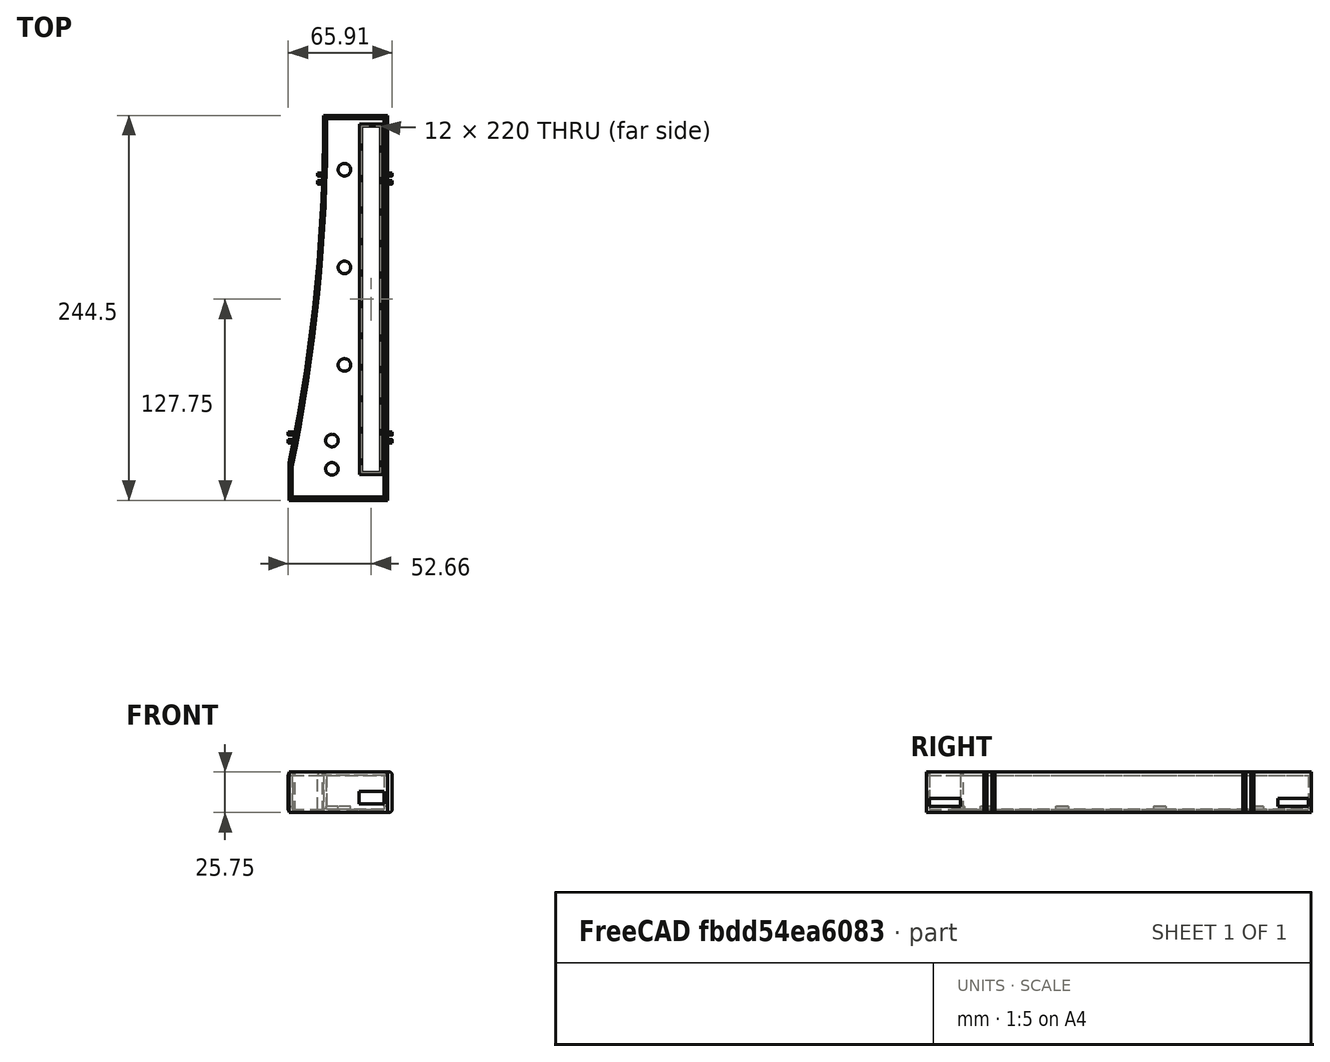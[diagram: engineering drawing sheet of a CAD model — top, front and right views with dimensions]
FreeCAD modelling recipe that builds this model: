
FCSTD DOCUMENT  (FreeCAD 0.19R)
Label: case-bottom
License: All rights reserved
LicenseURL: http://en.wikipedia.org/wiki/All_rights_reserved
objects: Sketcher::SketchObject×10, PartDesign::Pocket×7, PartDesign::Pad×3, Image::ImagePlane×1, PartDesign::Fillet×1, PartDesign::Body×1, Mesh::Feature×1
note: 33 computed .brp shape members not serialized (recipe doc carries the construction recipe); baked Part::Feature solids carry a one-line shape summary decoded from their .brp

FEATURE [Sketcher::SketchObject] Sketch
  FullyConstrained = true
  MapMode = 5
  Support = -> [XY_Plane]
  sketch-geometry (5):
    g0: LineSegment StartX=70.75 StartY=0 StartZ=0 EndX=70.75 EndY=244.5 EndZ=0
    g1: LineSegment StartX=70.75 StartY=244.5 StartZ=0 EndX=30.25 EndY=244.5 EndZ=0
    g2: LineSegment StartX=70.75 StartY=0 StartZ=0 EndX=8.25 EndY=0 EndZ=0
    g3: LineSegment StartX=8.25 StartY=0 StartZ=0 EndX=8.25 EndY=23.5 EndZ=0
    g4: ArcOfCircle CenterX=-1044.74 CenterY=239.918 CenterZ=0 NormalX=0 NormalY=0 NormalZ=1 AngleXU=0 Radius=1075 StartAngle=6.08048 EndAngle=6.28745
  constraints (16):
    c: PointOnObject(g0,g-1)
    c: Vertical(g0)
    c: Coincident(g1,g0)
    c: Horizontal(g1)
    c: Coincident(g2,g0)
    c: PointOnObject(g2,g-1)
    c: Coincident(g3,g2)
    c: Vertical(g3)
    c: Coincident(g4,g3)
    c: Coincident(g4,g1)
    c: DistanceX(g-1,g2) = 8.25
    c: DistanceX(g2,g2) = 62.5
    c: DistanceY(g0,g0) = 244.5
    c: DistanceX(g1,g1) = 40.5
    c: DistanceY(g3,g3) = 23.5
    c: Diameter(g4) = 2150
FEATURE [PartDesign::Pad] Pad
  Direction = (1,1,1)
  Length = 25.75
  Length2 = 100
  Profile = -> Sketch
  Type = 0
FEATURE [Sketcher::SketchObject] Sketch001
  FullyConstrained = true
  MapMode = 5
  Placement = pos=(0,0,25.75) rot=(0,0,1;0rad)
  Support = -> [Pad]
  sketch-geometry (5):
    g0: LineSegment StartX=10.25 StartY=2 StartZ=0 EndX=68.75 EndY=2 EndZ=0
    g1: LineSegment StartX=68.75 StartY=2 StartZ=0 EndX=68.75 EndY=242.5 EndZ=0
    g2: LineSegment StartX=68.75 StartY=242.5 StartZ=0 EndX=32.25 EndY=242.5 EndZ=0
    g3: ArcOfCircle CenterX=-1042.74 CenterY=237.918 CenterZ=0 NormalX=0 NormalY=0 NormalZ=1 AngleXU=0 Radius=1075 StartAngle=6.08048 EndAngle=6.28745
    g4: LineSegment StartX=10.25 StartY=2 StartZ=0 EndX=10.25 EndY=21.5 EndZ=0
  constraints (16):
    c: Horizontal(g0)
    c: Coincident(g1,g0)
    c: Vertical(g1)
    c: DistanceX(g-1,g0) = 10.25
    c: DistanceY(g-1,g0) = 2
    c: DistanceX(g0,g0) = 58.5
    c: Coincident(g2,g1)
    c: Horizontal(g2)
    c: Coincident(g3,g2)
    c: Coincident(g4,g0)
    c: Vertical(g4)
    c: Coincident(g3,g4)
    c: DistanceY(g1,g1) = 240.5
    c: DistanceX(g2,g2) = 36.5
    c: DistanceY(g4,g4) = 19.5
    c: Diameter(g3) = 2150
FEATURE [PartDesign::Pocket] Pocket
  BaseFeature = -> Pad
  Length = 23.75
  Length2 = 100
  Profile = -> Sketch001
  Type = 0
FEATURE [Image::ImagePlane] ImagePlane
  Placement = pos=(39.5,122.25,0) rot=(0,0,1;0rad)
  XSize = 74
  YSize = 240
FEATURE [Sketcher::SketchObject] Sketch002
  FullyConstrained = true
  MapMode = 5
  Placement = pos=(0,0,25.75) rot=(0,0,1;0rad)
  Support = -> [Pocket]
  sketch-geometry (4):
    g0: LineSegment StartX=8.25 StartY=2 StartZ=0 EndX=10.25 EndY=2 EndZ=0
    g1: LineSegment StartX=10.25 StartY=2 StartZ=0 EndX=10.25 EndY=21.5 EndZ=0
    g2: LineSegment StartX=10.25 StartY=21.5 StartZ=0 EndX=8.25 EndY=21.5 EndZ=0
    g3: LineSegment StartX=8.25 StartY=21.5 StartZ=0 EndX=8.25 EndY=2 EndZ=0
  constraints (12):
    c: Coincident(g0,g1)
    c: Coincident(g1,g2)
    c: Coincident(g2,g3)
    c: Coincident(g3,g0)
    c: Horizontal(g0)
    c: Horizontal(g2)
    c: Vertical(g1)
    c: Vertical(g3)
    c: DistanceX(g-1,g0) = 8.25
    c: DistanceY(g-1,g0) = 2
    c: DistanceX(g2,g2) = 2
    c: DistanceY(g1,g1) = 19.5
FEATURE [PartDesign::Pocket] Pocket001
  BaseFeature = -> Pocket
  Length = 21.75
  Length2 = 100
  Profile = -> Sketch002
  Type = 0
FEATURE [Sketcher::SketchObject] Sketch003
  FullyConstrained = true
  MapMode = 5
  Placement = pos=(70.75,0,0) rot=(0.57735,0.57735,0.57735;2.0944rad)
  Support = -> [Pocket001]
  sketch-geometry (8):
    g0: LineSegment StartX=2 StartY=4 StartZ=0 EndX=21.5 EndY=4 EndZ=0
    g1: LineSegment StartX=21.5 StartY=4 StartZ=0 EndX=21.5 EndY=9 EndZ=0
    g2: LineSegment StartX=21.5 StartY=9 StartZ=0 EndX=2 EndY=9 EndZ=0
    g3: LineSegment StartX=2 StartY=9 StartZ=0 EndX=2 EndY=4 EndZ=0
    g4: LineSegment StartX=242.5 StartY=4 StartZ=0 EndX=223 EndY=4 EndZ=0
    g5: LineSegment StartX=223 StartY=4 StartZ=0 EndX=223 EndY=9 EndZ=0
    g6: LineSegment StartX=223 StartY=9 StartZ=0 EndX=242.5 EndY=9 EndZ=0
    g7: LineSegment StartX=242.5 StartY=9 StartZ=0 EndX=242.5 EndY=4 EndZ=0
  constraints (24):
    c: Coincident(g0,g1)
    c: Coincident(g1,g2)
    c: Coincident(g2,g3)
    c: Coincident(g3,g0)
    c: Horizontal(g0)
    c: Horizontal(g2)
    c: Vertical(g1)
    c: Vertical(g3)
    c: Coincident(g4,g5)
    c: Coincident(g5,g6)
    c: Coincident(g6,g7)
    c: Coincident(g7,g4)
    c: Horizontal(g4)
    c: Horizontal(g6)
    c: Vertical(g5)
    c: Vertical(g7)
    c: DistanceX(g-1,g0) = 2
    c: DistanceY(g-1,g0) = 4
    c: DistanceX(g2,g2) = 19.5
    c: DistanceY(g1,g1) = 5
    c: DistanceY(g-1,g4) = 4
    c: DistanceX(g-1,g4) = 223
    c: DistanceX(g6,g6) = 19.5
    c: DistanceY(g7,g7) = 5
FEATURE [PartDesign::Pocket] Pocket002
  BaseFeature = -> Pocket001
  Length = 5
  Length2 = 100
  Profile = -> Sketch003
  Type = 2
FEATURE [Sketcher::SketchObject] Sketch004
  FullyConstrained = true
  MapMode = 5
  Placement = pos=(0,0,0) rot=(1,0,0;1.5708rad)
  Support = -> [Pocket002]
  sketch-geometry (4):
    g0: LineSegment StartX=68.75 StartY=5.5 StartZ=0 EndX=52.75 EndY=5.5 EndZ=0
    g1: LineSegment StartX=52.75 StartY=5.5 StartZ=0 EndX=52.75 EndY=13.5 EndZ=0
    g2: LineSegment StartX=52.75 StartY=13.5 StartZ=0 EndX=68.75 EndY=13.5 EndZ=0
    g3: LineSegment StartX=68.75 StartY=13.5 StartZ=0 EndX=68.75 EndY=5.5 EndZ=0
  constraints (12):
    c: Coincident(g0,g1)
    c: Coincident(g1,g2)
    c: Coincident(g2,g3)
    c: Coincident(g3,g0)
    c: Horizontal(g0)
    c: Horizontal(g2)
    c: Vertical(g1)
    c: Vertical(g3)
    c: DistanceY(g-1,g0) = 5.5
    c: DistanceX(g-1,g0) = 52.75
    c: DistanceY(g3,g3) = 8
    c: DistanceX(g2,g2) = 16
FEATURE [PartDesign::Pocket] Pocket003
  BaseFeature = -> Pocket002
  Length = 5
  Length2 = 100
  Profile = -> Sketch004
  Type = 2
FEATURE [Sketcher::SketchObject] Sketch005
  FullyConstrained = true
  MapMode = 5
  Placement = pos=(0,0,4) rot=(0,0,1;0rad)
  Support = -> [Pocket003]
  sketch-geometry (4):
    g0: LineSegment StartX=66.5 StartY=17.75 StartZ=0 EndX=54.5 EndY=17.75 EndZ=0
    g1: LineSegment StartX=54.5 StartY=17.75 StartZ=0 EndX=54.5 EndY=237.75 EndZ=0
    g2: LineSegment StartX=54.5 StartY=237.75 StartZ=0 EndX=66.5 EndY=237.75 EndZ=0
    g3: LineSegment StartX=66.5 StartY=237.75 StartZ=0 EndX=66.5 EndY=17.75 EndZ=0
  constraints (12):
    c: Coincident(g0,g1)
    c: Coincident(g1,g2)
    c: Coincident(g2,g3)
    c: Coincident(g3,g0)
    c: Horizontal(g0)
    c: Horizontal(g2)
    c: Vertical(g1)
    c: Vertical(g3)
    c: DistanceX(g2,g2) = 12
    c: DistanceY(g3,g3) = 220
    c: DistanceX(g-1,g0) = 54.5
    c: DistanceY(g-1,g0) = 17.75
FEATURE [PartDesign::Pocket] Pocket004
  BaseFeature = -> Pocket003
  Length = 5
  Length2 = 100
  Profile = -> Sketch005
  Type = 1
FEATURE [Sketcher::SketchObject] Sketch006
  FullyConstrained = true
  MapMode = 5
  Placement = pos=(0,0,2) rot=(0,0,1;0rad)
  Support = -> [Pocket004]
  sketch-geometry (4):
    g0: LineSegment StartX=67.75 StartY=16.5 StartZ=0 EndX=53.25 EndY=16.5 EndZ=0
    g1: LineSegment StartX=53.25 StartY=16.5 StartZ=0 EndX=53.25 EndY=239 EndZ=0
    g2: LineSegment StartX=53.25 StartY=239 StartZ=0 EndX=67.75 EndY=239 EndZ=0
    g3: LineSegment StartX=67.75 StartY=239 StartZ=0 EndX=67.75 EndY=16.5 EndZ=0
  constraints (12):
    c: Coincident(g0,g1)
    c: Coincident(g1,g2)
    c: Coincident(g2,g3)
    c: Coincident(g3,g0)
    c: Horizontal(g0)
    c: Horizontal(g2)
    c: Vertical(g1)
    c: Vertical(g3)
    c: DistanceX(g2,g2) = 14.5
    c: DistanceY(g3,g3) = 222.5
    c: DistanceX(g-1,g0) = 53.25
    c: DistanceY(g-1,g0) = 16.5
FEATURE [PartDesign::Pocket] Pocket005
  BaseFeature = -> Pocket004
  Length = 1.25
  Length2 = 100
  Profile = -> Sketch006
  Type = 0
FEATURE [Sketcher::SketchObject] Sketch007
  FullyConstrained = true
  MapMode = 5
  Placement = pos=(0,0,25.75) rot=(0,0,1;0rad)
  Support = -> [Pocket005]
  sketch-geometry (5):
    g0: LineSegment StartX=9.25 StartY=1 StartZ=0 EndX=9.25 EndY=22.5 EndZ=0
    g1: LineSegment StartX=9.25 StartY=1 StartZ=0 EndX=69.75 EndY=1 EndZ=0
    g2: LineSegment StartX=69.75 StartY=1 StartZ=0 EndX=69.75 EndY=243.5 EndZ=0
    g3: LineSegment StartX=69.75 StartY=243.5 StartZ=0 EndX=31.25 EndY=243.5 EndZ=0
    g4: ArcOfCircle CenterX=-1043.74 CenterY=238.918 CenterZ=0 NormalX=0 NormalY=0 NormalZ=1 AngleXU=0 Radius=1075 StartAngle=6.08048 EndAngle=6.28745
  constraints (16):
    c: Vertical(g0)
    c: Coincident(g1,g0)
    c: Horizontal(g1)
    c: Coincident(g2,g1)
    c: Vertical(g2)
    c: Coincident(g3,g2)
    c: Horizontal(g3)
    c: Coincident(g4,g0)
    c: Coincident(g4,g3)
    c: DistanceY(g-1,g0) = 1
    c: DistanceX(g-1,g0) = 9.25
    c: DistanceX(g1,g1) = 60.5
    c: DistanceY(g0,g0) = 21.5
    c: DistanceY(g2,g2) = 242.5
    c: DistanceX(g3,g3) = 38.5
    c: Diameter(g4) = 2150
FEATURE [PartDesign::Pocket] Pocket006
  BaseFeature = -> Pocket005
  Length = 2.25
  Length2 = 100
  Profile = -> Sketch007
  Type = 0
FEATURE [Sketcher::SketchObject] Sketch008
  FullyConstrained = true
  MapMode = 5
  Placement = pos=(0,0,2) rot=(0,0,1;0rad)
  Support = -> [Pocket006]
  sketch-geometry (8):
    g0: Circle CenterX=35.5 CenterY=38 CenterZ=0 NormalX=0 NormalY=0 NormalZ=1 AngleXU=0 Radius=4
    g1: Circle CenterX=43.5 CenterY=86 CenterZ=0 NormalX=0 NormalY=0 NormalZ=1 AngleXU=0 Radius=4
    g2: Circle CenterX=43.5 CenterY=148 CenterZ=0 NormalX=0 NormalY=0 NormalZ=1 AngleXU=0 Radius=4
    g3: Circle CenterX=43.5 CenterY=210 CenterZ=0 NormalX=0 NormalY=0 NormalZ=1 AngleXU=0 Radius=4
    g4: LineSegment StartX=0 StartY=12 StartZ=0 EndX=43.5 EndY=12 EndZ=0
    g5: LineSegment StartX=35.5 StartY=12 StartZ=0 EndX=35.5 EndY=38 EndZ=0
    g6: LineSegment StartX=43.5 StartY=12 StartZ=0 EndX=43.5 EndY=210 EndZ=0
    g7: Circle CenterX=35.5 CenterY=20 CenterZ=0 NormalX=0 NormalY=0 NormalZ=1 AngleXU=0 Radius=4
  constraints (24):
    c: Equal(g1,g2)
    c: Equal(g2,g3)
    c: PointOnObject(g4,g-2)
    c: Horizontal(g4)
    c: PointOnObject(g5,g4)
    c: Coincident(g5,g0)
    c: Vertical(g5)
    c: Coincident(g6,g4)
    c: Coincident(g6,g3)
    c: Vertical(g6)
    c: PointOnObject(g2,g6)
    c: PointOnObject(g1,g6)
    c: DistanceX(g4,g4) = 43.5
    c: DistanceY(g-1,g4) = 12
    c: PointOnObject(g7,g5)
    c: DistanceY(g5,g7) = 8
    c: Equal(g7,g0)
    c: Diameter(g7) = 8
    c: DistanceY(g5,g5) = 26
    c: DistanceX(g4,g5) = 35.5
    c: DistanceY(g6,g6) = 198
    c: DistanceY(g4,g1) = 74
    c: DistanceY(g4,g2) = 136
    c: Equal(g1,g0)
FEATURE [PartDesign::Pad] Pad001
  BaseFeature = -> Pocket006
  Direction = (1,1,1)
  Length = 1.75
  Length2 = 100
  Profile = -> Sketch008
  Type = 0
FEATURE [Sketcher::SketchObject] Sketch009
  FullyConstrained = true
  MapMode = 5
  Placement = pos=(0,0,0) rot=(1,0,0;3.14159rad)
  Support = -> [Pad001]
  sketch-geometry (47):
    g0: LineSegment StartX=8.25 StartY=0 StartZ=0 EndX=70.75 EndY=0 EndZ=0
    g1: LineSegment StartX=70.75 StartY=0 StartZ=0 EndX=70.75 EndY=-244.5 EndZ=0
    g2: LineSegment StartX=70.75 StartY=-244.5 StartZ=0 EndX=30.25 EndY=-244.5 EndZ=0
    g3: LineSegment StartX=8.25 StartY=0 StartZ=0 EndX=8.25 EndY=-23.5 EndZ=0
    g4: ArcOfCircle CenterX=-1044.74 CenterY=-239.918 CenterZ=0 NormalX=0 NormalY=0 NormalZ=1 AngleXU=0 Radius=1075 StartAngle=6.27892 EndAngle=6.48589
    g5: LineSegment StartX=70.75 StartY=-40 StartZ=0 EndX=11.5069 EndY=-40 EndZ=0
    g6: LineSegment StartX=70.75 StartY=-204.5 StartZ=0 EndX=29.6762 EndY=-204.5 EndZ=0
    g7: LineSegment StartX=70.75 StartY=-38.5 StartZ=0 EndX=73.75 EndY=-38.5 EndZ=0
    g8: LineSegment StartX=73.75 StartY=-38.5 StartZ=0 EndX=73.75 EndY=-36.5 EndZ=0
    g9: LineSegment StartX=73.75 StartY=-36.5 StartZ=0 EndX=70.75 EndY=-36.5 EndZ=0
    g10: LineSegment StartX=70.75 StartY=-36.5 StartZ=0 EndX=70.75 EndY=-38.5 EndZ=0
    g11: LineSegment StartX=70.75 StartY=-41.5 StartZ=0 EndX=73.75 EndY=-41.5 EndZ=0
    g12: LineSegment StartX=73.75 StartY=-41.5 StartZ=0 EndX=73.75 EndY=-43.5 EndZ=0
    g13: LineSegment StartX=73.75 StartY=-43.5 StartZ=0 EndX=70.75 EndY=-43.5 EndZ=0
    g14: LineSegment StartX=70.75 StartY=-43.5 StartZ=0 EndX=70.75 EndY=-41.5 EndZ=0
    g15: LineSegment StartX=11.2219 StartY=-38.5 StartZ=0 EndX=7.83842 EndY=-38.5 EndZ=0
    g16: LineSegment StartX=7.83842 StartY=-38.5 StartZ=0 EndX=7.83842 EndY=-36.5 EndZ=0
    g17: LineSegment StartX=7.83842 StartY=-36.5 StartZ=0 EndX=10.8384 EndY=-36.5 EndZ=0
    g18: LineSegment StartX=12.1633 StartY=-43.5 StartZ=0 EndX=7.83842 EndY=-43.5 EndZ=0
    g19: LineSegment StartX=7.83842 StartY=-43.5 StartZ=0 EndX=7.83842 EndY=-41.5 EndZ=0
    g20: LineSegment StartX=7.83842 StartY=-41.5 StartZ=0 EndX=11.7897 EndY=-41.5 EndZ=0
    g21: LineSegment StartX=7.83842 StartY=-41.5 StartZ=0 EndX=7.83842 EndY=-38.5 EndZ=0
    g22: ArcOfCircle CenterX=-1044.74 CenterY=-239.918 CenterZ=0 NormalX=0 NormalY=0 NormalZ=1 AngleXU=0 Radius=1075 StartAngle=0.188479 EndAngle=0.190373
    g23: ArcOfCircle CenterX=-1044.74 CenterY=-239.918 CenterZ=0 NormalX=0 NormalY=0 NormalZ=1 AngleXU=0 Radius=1075 StartAngle=0.183746 EndAngle=0.185639
    g24: LineSegment StartX=11.5069 StartY=-40 StartZ=0 EndX=7.83842 EndY=-40 EndZ=0
    g25: LineSegment StartX=73.75 StartY=-41.5 StartZ=0 EndX=73.75 EndY=-38.5 EndZ=0
    g26: LineSegment StartX=70.75 StartY=-40 StartZ=0 EndX=73.75 EndY=-40 EndZ=0
    g27: LineSegment StartX=70.75 StartY=-204.5 StartZ=0 EndX=73.75 EndY=-204.5 EndZ=0
    g28: LineSegment StartX=73.75 StartY=-206 StartZ=0 EndX=73.75 EndY=-203 EndZ=0
    g29: LineSegment StartX=29.6762 StartY=-204.5 StartZ=0 EndX=26.5551 EndY=-204.5 EndZ=0
    g30: LineSegment StartX=26.5551 StartY=-206 StartZ=0 EndX=26.5551 EndY=-203 EndZ=0
    g31: LineSegment StartX=73.75 StartY=-203 StartZ=0 EndX=70.75 EndY=-203 EndZ=0
    g32: LineSegment StartX=70.75 StartY=-203 StartZ=0 EndX=70.75 EndY=-201 EndZ=0
    g33: LineSegment StartX=70.75 StartY=-201 StartZ=0 EndX=73.75 EndY=-201 EndZ=0
    g34: LineSegment StartX=73.75 StartY=-201 StartZ=0 EndX=73.75 EndY=-203 EndZ=0
    g35: LineSegment StartX=73.75 StartY=-206 StartZ=0 EndX=70.75 EndY=-206 EndZ=0
    g36: LineSegment StartX=70.75 StartY=-206 StartZ=0 EndX=70.75 EndY=-208 EndZ=0
    g37: LineSegment StartX=70.75 StartY=-208 StartZ=0 EndX=73.75 EndY=-208 EndZ=0
    g38: LineSegment StartX=73.75 StartY=-208 StartZ=0 EndX=73.75 EndY=-206 EndZ=0
    g39: LineSegment StartX=26.5551 StartY=-203 StartZ=0 EndX=29.6257 EndY=-203 EndZ=0
    g40: LineSegment StartX=29.5551 StartY=-201 StartZ=0 EndX=26.5551 EndY=-201 EndZ=0
    g41: LineSegment StartX=26.5551 StartY=-201 StartZ=0 EndX=26.5551 EndY=-203 EndZ=0
    g42: LineSegment StartX=26.5551 StartY=-206 StartZ=0 EndX=29.7246 EndY=-206 EndZ=0
    g43: LineSegment StartX=29.7858 StartY=-208 StartZ=0 EndX=26.5551 EndY=-208 EndZ=0
    g44: LineSegment StartX=26.5551 StartY=-208 StartZ=0 EndX=26.5551 EndY=-206 EndZ=0
    g45: ArcOfCircle CenterX=-1044.74 CenterY=-239.918 CenterZ=0 NormalX=0 NormalY=0 NormalZ=1 AngleXU=0 Radius=1075 StartAngle=0.0343487 EndAngle=0.0362103
    g46: ArcOfCircle CenterX=-1044.74 CenterY=-239.918 CenterZ=0 NormalX=0 NormalY=0 NormalZ=1 AngleXU=0 Radius=1075 StartAngle=0.0296951 EndAngle=0.0315565
  constraints (140):
    c: PointOnObject(g0,g-1)
    c: PointOnObject(g0,g-1)
    c: Coincident(g1,g0)
    c: Vertical(g1)
    c: Coincident(g2,g1)
    c: Horizontal(g2)
    c: Coincident(g3,g0)
    c: Vertical(g3)
    c: Coincident(g4,g3)
    c: Coincident(g4,g2)
    c: DistanceX(g-1,g0) = 8.25
    c: DistanceX(g0,g0) = 62.5
    c: DistanceY(g3,g3) = 23.5
    c: DistanceY(g1,g1) = 244.5
    c: DistanceX(g2,g2) = 40.5
    c: Diameter(g4) = 2150
    c: PointOnObject(g5,g1)
    c: PointOnObject(g5,g4)
    c: Horizontal(g5)
    c: DistanceY(g5,g0) = 40
    c: PointOnObject(g6,g1)
    c: PointOnObject(g6,g4)
    c: Horizontal(g6)
    c: DistanceY(g1,g6) = 40
    c: Coincident(g7,g8)
    c: Coincident(g8,g9)
    c: Coincident(g9,g10)
    c: Coincident(g10,g7)
    c: Horizontal(g7)
    c: Horizontal(g9)
    c: Vertical(g8)
    c: Vertical(g10)
    c: PointOnObject(g7,g1)
    c: Coincident(g11,g12)
    c: Coincident(g12,g13)
    c: Coincident(g13,g14)
    c: Coincident(g14,g11)
    c: Horizontal(g11)
    c: Horizontal(g13)
    c: Vertical(g12)
    c: Vertical(g14)
    c: PointOnObject(g11,g1)
    c: Coincident(g15,g16)
    c: Coincident(g16,g17)
    c: Horizontal(g15)
    c: Horizontal(g17)
    c: Vertical(g16)
    c: PointOnObject(g15,g4)
    c: Coincident(g18,g19)
    c: Coincident(g19,g20)
    c: Horizontal(g18)
    c: Horizontal(g20)
    c: Vertical(g19)
    c: PointOnObject(g18,g4)
    c: Coincident(g21,g19)
    c: Coincident(g21,g15)
    c: Vertical(g21)
    c: PointOnObject(g17,g4)
    c: PointOnObject(g20,g4)
    c: Coincident(g22,g17)
    c: Coincident(g22,g15)
    c: Coincident(g23,g18)
    c: Coincident(g23,g20)
    c: Diameter(g22) = 2150
    c: Diameter(g23) = 2150
    c: Equal(g19,g16)
    c: Coincident(g24,g5)
    c: Horizontal(g24)
    c: Symmetric(g19,g15,g24)
    c: DistanceX(g17,g17) = 3
    c: DistanceY(g16,g16) = 2
    c: DistanceY(g21,g21) = 3
    c: Coincident(g25,g11)
    c: Coincident(g25,g7)
    c: Coincident(g26,g5)
    c: Horizontal(g26)
    c: Vertical(g25)
    c: Symmetric(g11,g7,g26)
    c: Coincident(g27,g6)
    c: Horizontal(g27)
    c: Vertical(g28)
    c: Coincident(g29,g6)
    c: Horizontal(g29)
    c: Vertical(g30)
    c: Symmetric(g28,g28,g27)
    c: Symmetric(g30,g30,g29)
    c: Coincident(g31,g32)
    c: Coincident(g32,g33)
    c: Coincident(g33,g34)
    c: Coincident(g34,g31)
    c: Horizontal(g31)
    c: Horizontal(g33)
    c: Vertical(g32)
    c: Vertical(g34)
    c: Coincident(g31,g28)
    c: PointOnObject(g32,g1)
    c: Coincident(g35,g36)
    c: Coincident(g36,g37)
    c: Coincident(g37,g38)
    c: Coincident(g38,g35)
    c: Horizontal(g35)
    c: Horizontal(g37)
    c: Vertical(g36)
    c: Vertical(g38)
    c: Coincident(g35,g28)
    c: PointOnObject(g36,g1)
    c: Coincident(g40,g41)
    c: Coincident(g41,g39)
    c: Horizontal(g39)
    c: Horizontal(g40)
    c: Vertical(g41)
    c: Coincident(g39,g30)
    c: Coincident(g43,g44)
    c: Coincident(g44,g42)
    c: Horizontal(g42)
    c: Horizontal(g43)
    c: Vertical(g44)
    c: Coincident(g42,g30)
    c: PointOnObject(g43,g4)
    c: PointOnObject(g39,g4)
    c: PointOnObject(g42,g4)
    c: PointOnObject(g40,g4)
    c: Coincident(g45,g40)
    c: Coincident(g45,g39)
    c: Coincident(g46,g42)
    c: Coincident(g46,g43)
    c: Diameter(g45) = 2150
    c: Diameter(g46) = 2150
    c: Equal(g16,g8)
    c: Equal(g8,g12)
    c: Equal(g12,g34)
    c: Equal(g34,g38)
    c: Equal(g38,g41)
    c: Equal(g41,g44)
    c: Equal(g21,g25)
    c: Equal(g25,g28)
    c: Equal(g28,g30)
    c: Equal(g17,g9)
    c: Equal(g9,g33)
    c: Equal(g33,g40)
FEATURE [PartDesign::Pad] Pad002
  BaseFeature = -> Pad001
  Direction = (1,1,1)
  Length = 25.75
  Length2 = 100
  Profile = -> Sketch009
  Reversed = true
  Type = 0
FEATURE [PartDesign::Fillet] Fillet
  Base = -> Pad002 [Edge161,Edge158,Edge109,Edge114,Edge120,Edge124,Edge165,Edge167,Edge84,Edge80,Edge170,Edge136,Edge90,Edge95,Edge174,Edge177]
  BaseFeature = -> Pad002
  Radius = 2
  SupportTransform = false
FEATURE [PartDesign::Body] Body
  Group = -> [Sketch,Pad,Sketch001,Pocket,Sketch002,Pocket001,Sketch003,Pocket002,Sketch004,Pocket003,Sketch005,Pocket004,Sketch006,Pocket005,Sketch007,Pocket006,Sketch008,Pad001,Sketch009,Pad002,Fillet]
  Origin = -> Origin
  Tip = -> Fillet
FEATURE [Mesh::Feature] Mesh  label="Body (Meshed)"
